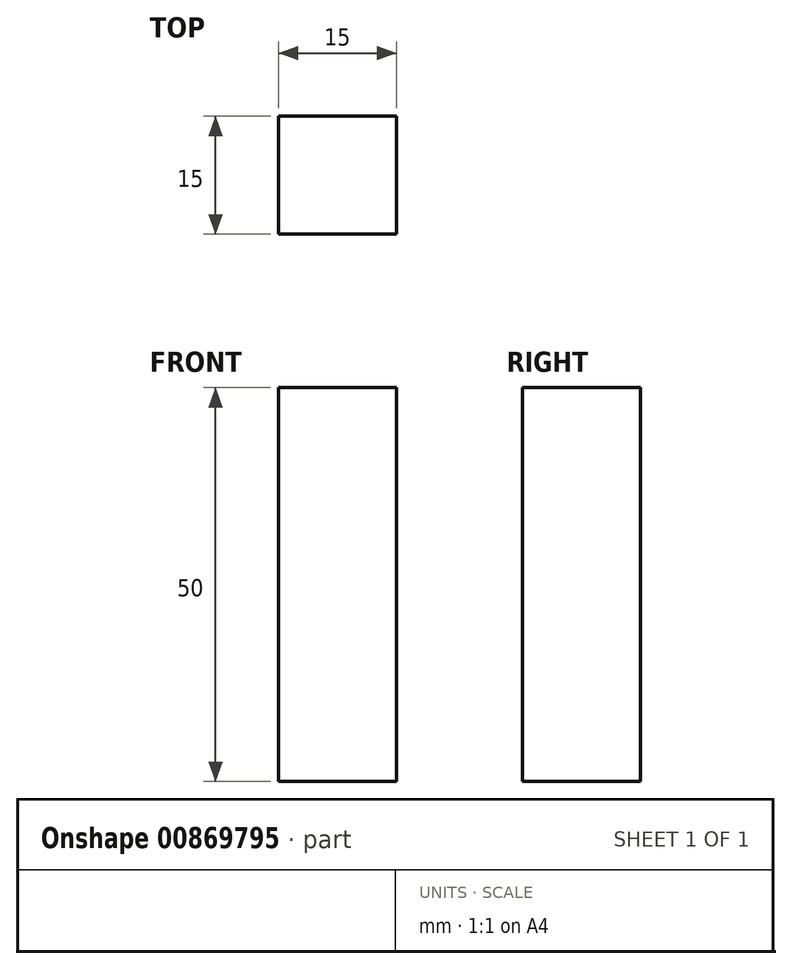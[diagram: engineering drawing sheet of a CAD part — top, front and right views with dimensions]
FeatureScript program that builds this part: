
annotation { "Feature Type Name" : "Feature", "Feature Type Description" : "" }
export const myFeature = defineFeature(function(context is Context, id is Id, definition is map)
    precondition{}
    {
        {
            var Q0;
            Q0=qCreatedBy(makeId("Top.planeOp"),FACE);
            var sketch = newSketch(context, id + "F0", { "sketchPlane" : qUnion([Q0])});
            skLineSegment(sketch, "E0.bottom", {"start": v(-7.5, 15) * mm, "end": v(7.5, 15) * mm});
            skLineSegment(sketch, "E0.top", {"start": v(-7.5, 0) * mm, "end": v(7.5, 0) * mm});
            skLineSegment(sketch, "E0.left", {"start": v(-7.5, 15) * mm, "end": v(-7.5, 0) * mm});
            skLineSegment(sketch, "E0.right", {"start": v(7.5, 15) * mm, "end": v(7.5, 0) * mm});
            skPoint(sketch, "E0.middle", {"position": v(0, 7.5) * mm});
            skSolve(sketch);
        }
        {
            var Q0;
            Q0 = qSketchRegion(id + "F0", true);
            extrude(context, id + "F1", {"entities" : qUnion([Q0]), "depth" : 50 * mm, "offsetDistance" : 25 * mm});
        }
    });
